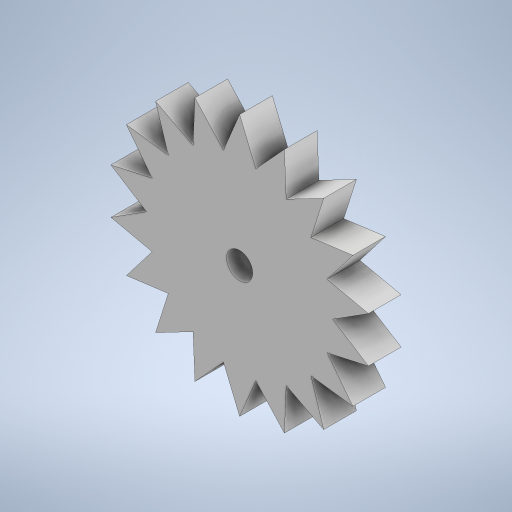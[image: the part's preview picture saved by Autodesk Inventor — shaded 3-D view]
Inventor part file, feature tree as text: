
AUTODESK INVENTOR PART (.ipt)
format: ipt  version: 2023 (Build 270158030, 158C)  size: 288,256 bytes
history: native  units: in
note: dims shown in document units (in); Inventor stores cm internally (conversion verified against a paired STEP export)
features: sketch x3, extrude x2, pattern_circular x1, hole x1
ambient origin geometry x8: Origin, YZ Plane, XZ Plane, XY Plane, X Axis, Y Axis, Z Axis, Center Point
bodies: Solid1 (feature_tree)
feature tree (7):
  extrude  "Extrusion1"  Depth=0.1969in TaperAngle=0.0deg
  extrude  "Extrusion2"  Depth=0.3937in
  pattern_circular  "Circular Pattern1"  Count=18 Angle=360.0deg
  hole  "Hole1"  [1 undecoded]
  sketch  "Sketch2"  dims[d0=0.7874in d1=0.1969in d2=0.0in]
  sketch  "Sketch3"  dims[d3=45.0deg d4=0.3937in]
  sketch  "Sketch4"  dims[d5=0.0in d6=0.0in d7=7.0866in d8=360.0deg d10=0.1575in d11=0.6299in d12=0.1575in d13=0.0787in d14=90.0deg d15=1.0748in d16=0.8108in]
note: 1 required parameter value undecoded (feature->parameter linkage not recoverable at this tier; creation-order binding heuristic only, values carry confidence <= 0.55)
